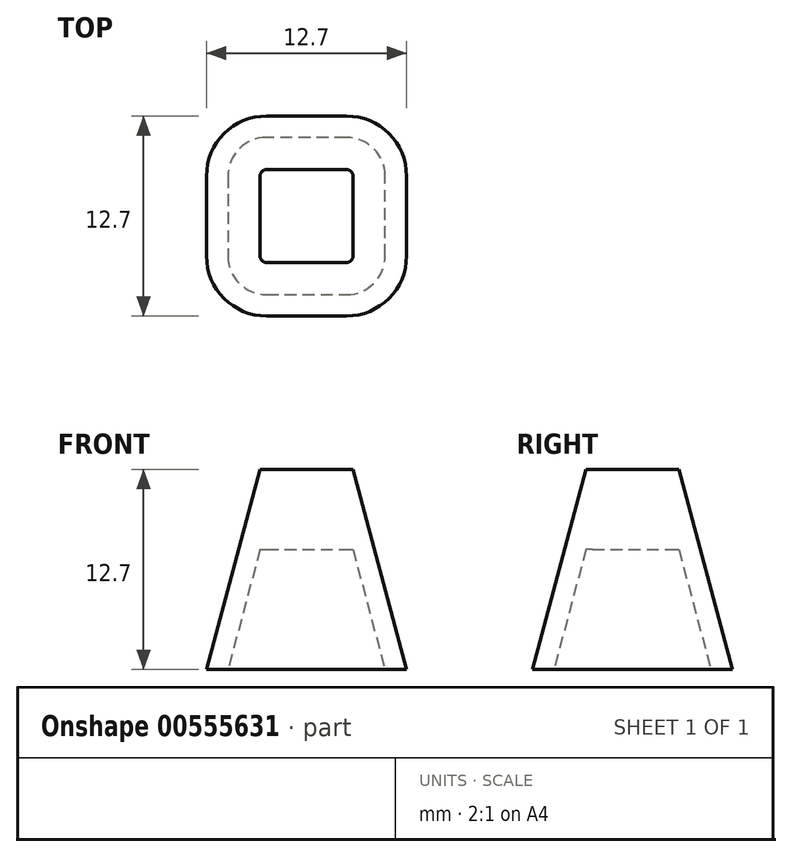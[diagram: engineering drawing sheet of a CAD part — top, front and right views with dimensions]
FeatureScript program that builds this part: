
annotation { "Feature Type Name" : "Feature", "Feature Type Description" : "" }
export const myFeature = defineFeature(function(context is Context, id is Id, definition is map)
    precondition{}
    {
        {
            var Q0;
            Q0=qCreatedBy(makeId("Top.planeOp"),FACE);
            var sketch = newSketch(context, id + "F0", { "sketchPlane" : qUnion([Q0])});
            skLineSegment(sketch, "E0.bottom", {"start": v(2.54, 6.35) * mm, "end": v(-2.54, 6.35) * mm});
            skLineSegment(sketch, "E0.top", {"start": v(2.54, -6.35) * mm, "end": v(-2.54, -6.35) * mm});
            skLineSegment(sketch, "E0.left", {"start": v(6.35, 2.54) * mm, "end": v(6.35, -2.54) * mm});
            skLineSegment(sketch, "E0.right", {"start": v(-6.35, 2.54) * mm, "end": v(-6.35, -2.54) * mm});
            skPoint(sketch, "E0.middle", {"position": v(0, 0) * mm});
            skPoint(sketch, "E1.visualSharp", {"position": v(6.35, 6.35) * mm});
            skArc(sketch, "E1.filletArc", {"start": v(6.35, 2.54) * mm, "mid": v(5.23, 5.23) * mm, "end": v(2.54, 6.35) * mm});
            skPoint(sketch, "E2.visualSharp", {"position": v(6.35, -6.35) * mm});
            skArc(sketch, "E2.filletArc", {"start": v(2.54, -6.35) * mm, "mid": v(5.23, -5.23) * mm, "end": v(6.35, -2.54) * mm});
            skPoint(sketch, "E3.visualSharp", {"position": v(-6.35, -6.35) * mm});
            skArc(sketch, "E3.filletArc", {"start": v(-6.35, -2.54) * mm, "mid": v(-5.23, -5.23) * mm, "end": v(-2.54, -6.35) * mm});
            skPoint(sketch, "E4.visualSharp", {"position": v(-6.35, 6.35) * mm});
            skArc(sketch, "E4.filletArc", {"start": v(-2.54, 6.35) * mm, "mid": v(-5.23, 5.23) * mm, "end": v(-6.35, 2.54) * mm});
            skSolve(sketch);
        }
        {
            var Q0;
            Q0 = qSketchRegion(id + "F0", true);
            extrude(context, id + "F1", {"entities" : qUnion([Q0]), "depth" : 12.7 * mm, "offsetDistance" : 25.4 * mm, "hasDraft" : true, "draftAngle" : 15 * degree, "draftPullDirection" : true});
        }
        {
            var Q0;
            Q0=makeQuery(id+"F1.opExtrude","CAP_FACE",FACE,{"disambiguationData":[OSD([sQuery(id+"F0.wireOp",EDGE,"E0.bottom"),sQuery(id+"F0.wireOp",EDGE,"E0.top"),sQuery(id+"F0.wireOp",EDGE,"E0.left"),sQuery(id+"F0.wireOp",EDGE,"E0.right"),sQuery(id+"F0.wireOp",EDGE,"E1.filletArc"),sQuery(id+"F0.wireOp",EDGE,"E2.filletArc"),sQuery(id+"F0.wireOp",EDGE,"E3.filletArc"),sQuery(id+"F0.wireOp",EDGE,"E4.filletArc")])],"isStart":false});
            cPlane(context, id + "F2", {"entities" : qUnion([Q0]), "cplaneType" : CPlaneType.OFFSET, "offset" : 5.08 * mm, "oppositeDirection" : true, "width" : 152.4 * mm, "height" : 152.4 * mm});
        }
        {
            var Q0;
            Q0=qCreatedBy(id+"F2.planeOp",FACE);
            var sketch = newSketch(context, id + "F3", { "sketchPlane" : qUnion([Q0])});
            skLineSegment(sketch, "E5.0.0", {"start": v(-2.54, -2.95) * mm, "end": v(2.54, -2.95) * mm});
            skArc(sketch, "E5.0.1", {"start": v(2.54, -2.95) * mm, "mid": v(2.83, -2.83) * mm, "end": v(2.95, -2.54) * mm});
            skLineSegment(sketch, "E5.0.2", {"start": v(2.95, -2.54) * mm, "end": v(2.95, 2.54) * mm});
            skArc(sketch, "E5.0.3", {"start": v(2.95, 2.54) * mm, "mid": v(2.83, 2.83) * mm, "end": v(2.54, 2.95) * mm});
            skLineSegment(sketch, "E5.0.4", {"start": v(2.54, 2.95) * mm, "end": v(-2.54, 2.95) * mm});
            skArc(sketch, "E5.0.5", {"start": v(-2.54, 2.95) * mm, "mid": v(-2.83, 2.83) * mm, "end": v(-2.95, 2.54) * mm});
            skLineSegment(sketch, "E5.0.6", {"start": v(-2.95, 2.54) * mm, "end": v(-2.95, -2.54) * mm});
            skArc(sketch, "E5.0.7", {"start": v(-2.95, -2.54) * mm, "mid": v(-2.83, -2.83) * mm, "end": v(-2.54, -2.95) * mm});
            skSolve(sketch);
        }
        {
            var Q0;
            Q0 = qSketchRegion(id + "F3", true);
            extrude(context, id + "F4", {"entities" : qUnion([Q0]), "operationType" : NewBodyOperationType.REMOVE, "oppositeDirection" : true, "depth" : 25.4 * mm, "offsetDistance" : 25.4 * mm, "hasDraft" : true, "draftAngle" : 15 * degree});
        }
    });
